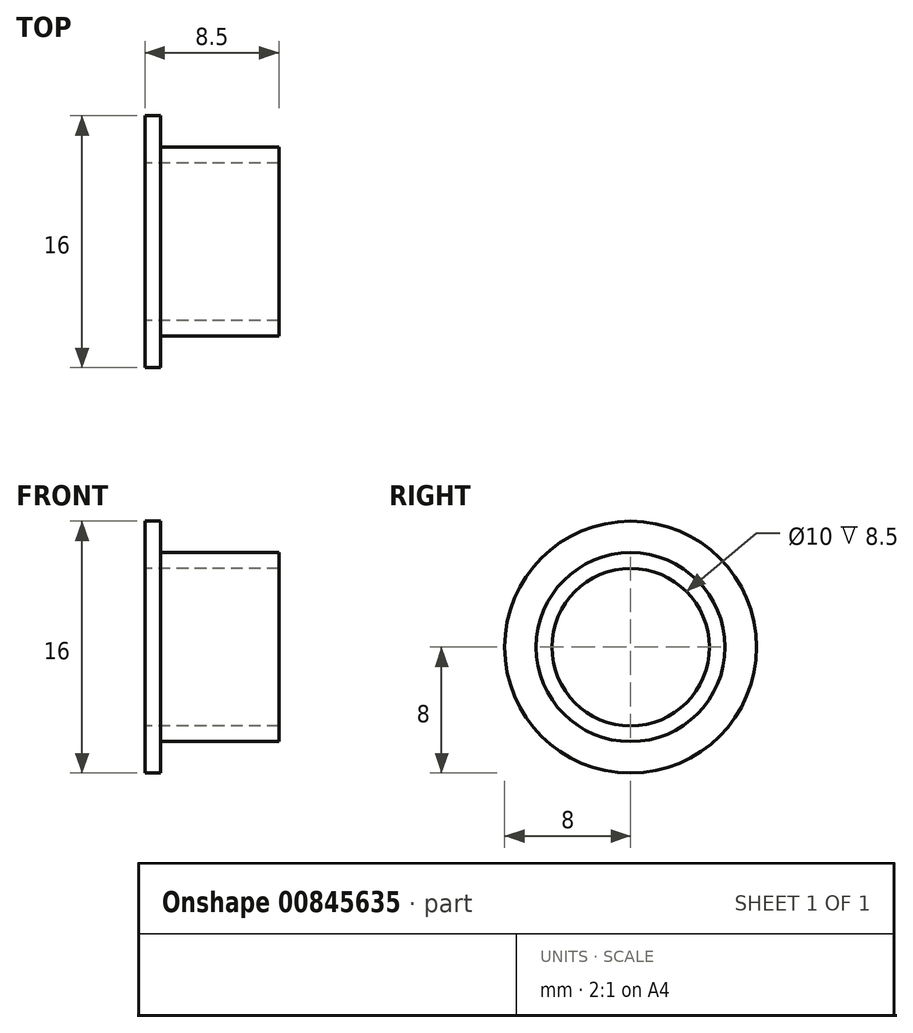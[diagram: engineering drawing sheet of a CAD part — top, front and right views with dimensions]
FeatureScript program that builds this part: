
annotation { "Feature Type Name" : "Feature", "Feature Type Description" : "" }
export const myFeature = defineFeature(function(context is Context, id is Id, definition is map)
    precondition{}
    {
        {
            var Q0;
            Q0=qCreatedBy(makeId("Front.planeOp"),FACE);
            var sketch = newSketch(context, id + "F0", { "sketchPlane" : qUnion([Q0])});
            skLineSegment(sketch, "E0", {"start": v(-1, 8) * mm, "end": v(0, 8) * mm});
            skLineSegment(sketch, "E1", {"start": v(0, 8) * mm, "end": v(0, 6) * mm});
            skLineSegment(sketch, "E2", {"start": v(0, 6) * mm, "end": v(7.5, 6) * mm});
            skLineSegment(sketch, "E3", {"start": v(7.5, 6) * mm, "end": v(7.5, 5) * mm});
            skLineSegment(sketch, "E4", {"start": v(7.5, 5) * mm, "end": v(-1, 5) * mm});
            skLineSegment(sketch, "E5", {"start": v(-1, 5) * mm, "end": v(-1, 8) * mm});
            skLineSegment(sketch, "E6", {"start": v(-1, 0) * mm, "end": v(7.5, 0) * mm, "construction": true});
            skSolve(sketch);
        }
        {
            var Q0;
            Q0=makeQuery(id+"F0.imprint","IMPRINT",FACE,{"disambiguationData":[TD([[makeQuery(id+"F0.imprint","IMPRINT",EDGE,{"derivedFrom":sQuery(id+"F0.wireOp",EDGE,"E0")}),-1.0]])]});
            var Q1;
            Q1=sQuery(id+"F0.wireOp",EDGE,"E6");
            revolve(context, id + "F1", {"surfaceOperationType" : NewSurfaceOperationType.NEW, "entities" : qUnion([Q0]), "axis" : qUnion([Q1]), "revolveType" : RevolveType.FULL});
        }
    });
